# Revit family: LowerUnit-Vitra-EqualSeries-64107+64108+64109+64110+64111+64112
name_source: partatom
category: Furniture Systems
revit_build: Autodesk Revit 2017 (Build: 20160225_1515(x64)
units: mm (PartAtom-declared; Revit-internal decimal feet)

## family parameters
Cut with Voids When Loaded = No
Host = Face
OmniClass Number = 23.40.00.00
OmniClass Title = Equipment and Furnishings
Part Type = Normal
Room Calculation Point = No
Round Connector Dimension = Use Diameter
Shared = Yes

## types (6) — shared parameters
BIMobject category = Storage
Construction Type = Face Mounted
Default Elevation = 660 mm
Depth(mm) = 420 mm  [stored 1.37795 ft]
Description = Equal Lower Unit,
Design country = Turkey
Height(mm) = 450 mm  [stored 1.47638 ft]
IFC Classification = Furniture
Left = No
Manufacturer = Vitra
Manufacturer name = Vitra
Masterformat 2014 Code = 12 35 30.23
Masterformat 2014 Description = Bathroom Casework
NBS Referans Code = 35-75-08
NBS Referans Description = Bathroom Cabinets
Nominal height = 0.000
Nominal width = 0.000
OmniClass Code = 23-31 25 13
OmniClass Description = Bathroom Cabinets
Product certification = https://vitraglobal.com
Product data url = https://www.vitraglobal.com
Product family = Equal
Product group = Bathroom Furniture
Right = No
Technical description = https://www.vitra.com.tr
UNSPSC Code = 30161801
UNSPSC Description = Bathroom Cabinets
URL = https://vitraglobal.com
Uniclass 1.4 Code = L8241
Uniclass 1.4 Description = Bathroom Cabinets
Uniclass 2.0 Code = PR-35-75-08
Uniclass 2.0 Description = Bathroom Cabinets
Uniclass 2015 Code = Pr_40_30_78_03
Uniclass 2015 Name = Bathroom Cabinets
Uniformat II Code = E2010
Uniformat II Description = Fixed Furnishings
Warranty Period (Year) = 2
Youtube = https://www.youtube.com

## per-type parameters (varying)
| type | Article No. (default) | Model | Primary Material | Product SKU | Weight Net (kg) | Width(mm) |
| LowerUnit-60cm-PatternedBlackOak-Vitra-EqualSeries_64107 | 64107 | 64107 | Vitra-BlackOak | 64107 | 20,000 | 600 mm |
| LowerUnit-60cm-Elm-Vitra-EqualSeries_64108 | 64108 | 64108 | Vitra-Elm | 64108 | 20,000 | 600 mm |
| LowerUnit-80cm-PatternedBlackOak-Vitra-EqualSeries_64109 | 64109 | 64109 | Vitra-BlackOak | 64109 | 26,000 | 800 mm  [stored 2.62467 ft] |
| LowerUnit-80cm-Elm-Vitra-EqualSeries_64110 | 64110 | 64110 | Vitra-Elm | 64110 | 26,000 | 800 mm  [stored 2.62467 ft] |
| LowerUnit-100cm-PatternedBlackOak-Vitra-EqualSeries_64111 | 64111 | 64111 | Vitra-BlackOak | 64111 | 31,000 | 1000 mm  [stored 3.28084 ft] |
| LowerUnit-100cm-Elm-Vitra-EqualSeries_64112 | 64112 | 64112 | Vitra-Elm | 64112 | 31,000 | 1000 mm  [stored 3.28084 ft] |

note: [stored X ft] marks values corroborated as IEEE doubles in the binary element streams (Revit-internal decimal feet)

## geometry (parser evidence)
native form markers: Sweep x3
no freeform markers — native parametric forms only
